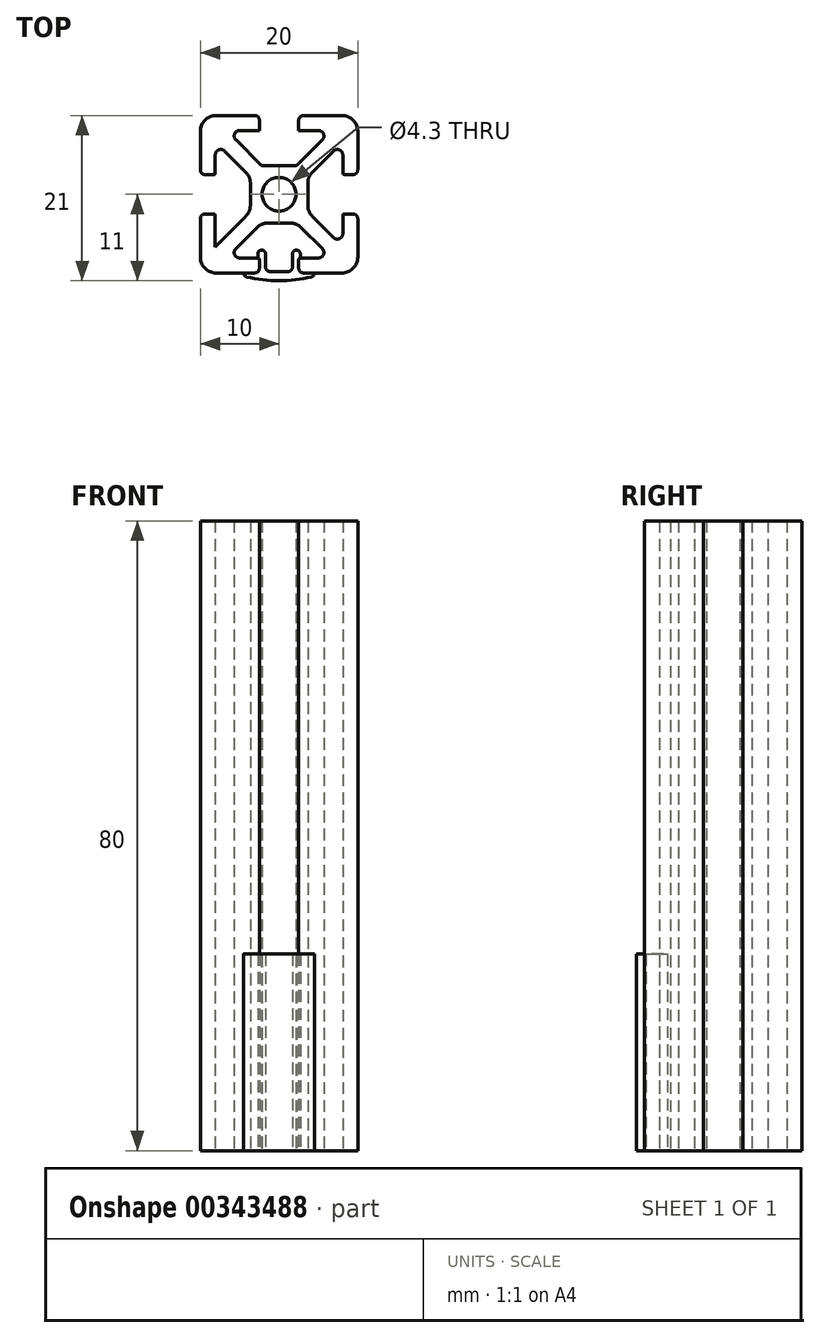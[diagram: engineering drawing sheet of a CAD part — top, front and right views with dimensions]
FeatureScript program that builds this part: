
annotation { "Feature Type Name" : "Feature", "Feature Type Description" : "" }
export const myFeature = defineFeature(function(context is Context, id is Id, definition is map)
    precondition{}
    {
        {
            var Q0;
            Q0=qCreatedBy(makeId("Top.planeOp"),FACE);
            var sketch = newSketch(context, id + "F0", { "sketchPlane" : qUnion([Q0])});
            skLineSegment(sketch, "E0.bottom", {"start": v(-8, 10) * mm, "end": v(-3.1, 10) * mm});
            skLineSegment(sketch, "E0.top", {"start": v(-8, -10) * mm, "end": v(-3.1, -10) * mm});
            skLineSegment(sketch, "E0.left", {"start": v(-10, 8) * mm, "end": v(-10, 3.1) * mm});
            skLineSegment(sketch, "E0.right", {"start": v(10, 8) * mm, "end": v(10, 3.1) * mm});
            skLineSegment(sketch, "E1", {"start": v(-10, 10) * mm, "end": v(10, -10) * mm, "construction": true});
            skLineSegment(sketch, "E2", {"start": v(10, 10) * mm, "end": v(-10, -10) * mm, "construction": true});
            skCircle(sketch, "E3", {"center": v(0, 0) * mm, "radius": 2.15 * mm});
            skLineSegment(sketch, "E4.bottom", {"start": v(-2.24, 3.65) * mm, "end": v(2.24, 3.65) * mm});
            skLineSegment(sketch, "E4.top", {"start": v(-1.4, -3.65) * mm, "end": v(1.4, -3.65) * mm});
            skLineSegment(sketch, "E4.left", {"start": v(-3.65, 1.4) * mm, "end": v(-3.65, -1.4) * mm});
            skLineSegment(sketch, "E4.right", {"start": v(3.65, 1.4) * mm, "end": v(3.65, -1.4) * mm});
            skLineSegment(sketch, "E5", {"start": v(-5.5, 6.9) * mm, "end": v(-2.24, 3.65) * mm});
            skLineSegment(sketch, "E6", {"start": v(-6.9, 5.5) * mm, "end": v(-4.24, 2.82) * mm});
            skLineSegment(sketch, "E7", {"start": v(5.5, 6.9) * mm, "end": v(2.24, 3.65) * mm});
            skLineSegment(sketch, "E8", {"start": v(6.9, 5.5) * mm, "end": v(4.24, 2.82) * mm});
            skLineSegment(sketch, "E9", {"start": v(-21.63, 0) * mm, "end": v(22.23, 0) * mm, "construction": true});
            skLineSegment(sketch, "E10.trimOffspring", {"start": v(-4.24, -2.82) * mm, "end": v(-8.1, -6.69) * mm});
            skLineSegment(sketch, "E11.trimOffspring", {"start": v(-2.82, -4.24) * mm, "end": v(-5.5, -6.9) * mm});
            skLineSegment(sketch, "E12.trimOffspring", {"start": v(2.82, -4.24) * mm, "end": v(5.5, -6.9) * mm});
            skLineSegment(sketch, "E13.trimOffspring", {"start": v(4.24, -2.82) * mm, "end": v(6.9, -5.5) * mm});
            skLineSegment(sketch, "E14", {"start": v(-8.1, 5) * mm, "end": v(-8.1, 2.7) * mm});
            skLineSegment(sketch, "E15", {"start": v(-8.3, 2.5) * mm, "end": v(-9.4, 2.5) * mm});
            skLineSegment(sketch, "E16", {"start": v(-8.3, -2.5) * mm, "end": v(-9.4, -2.5) * mm});
            skLineSegment(sketch, "E17.trimOffspring", {"start": v(-10, -3.1) * mm, "end": v(-10, -8) * mm});
            skLineSegment(sketch, "E18.trimOffspring", {"start": v(-8.1, -2.7) * mm, "end": v(-8.1, -6.69) * mm});
            skLineSegment(sketch, "E19", {"start": v(-5, 8.1) * mm, "end": v(-2.5, 8.1) * mm});
            skLineSegment(sketch, "E20", {"start": v(8.1, 5) * mm, "end": v(8.1, 2.7) * mm});
            skLineSegment(sketch, "E21", {"start": v(5, -8.1) * mm, "end": v(2.7, -8.1) * mm});
            skLineSegment(sketch, "E22", {"start": v(8.3, 2.5) * mm, "end": v(9.4, 2.5) * mm});
            skLineSegment(sketch, "E23", {"start": v(9.4, -2.5) * mm, "end": v(8.3, -2.5) * mm});
            skLineSegment(sketch, "E24.trimOffspring", {"start": v(10, -3.1) * mm, "end": v(10, -8) * mm});
            skLineSegment(sketch, "E25.trimOffspring", {"start": v(8.1, -2.7) * mm, "end": v(8.1, -5) * mm});
            skLineSegment(sketch, "E26", {"start": v(-2.5, 8.1) * mm, "end": v(-2.5, 9.4) * mm});
            skLineSegment(sketch, "E27", {"start": v(2.5, 8.1) * mm, "end": v(2.5, 9.4) * mm});
            skLineSegment(sketch, "E28", {"start": v(0, 10.9) * mm, "end": v(0, -13.43) * mm, "construction": true});
            skLineSegment(sketch, "E29.trimOffspring", {"start": v(3.1, 10) * mm, "end": v(8, 10) * mm});
            skLineSegment(sketch, "E30.trimOffspring", {"start": v(2.5, 8.1) * mm, "end": v(5, 8.1) * mm});
            skPoint(sketch, "E31.visualSharp", {"position": v(-10, 10) * mm});
            skArc(sketch, "E31.filletArc", {"start": v(-8, 10) * mm, "mid": v(-9.41, 9.41) * mm, "end": v(-10, 8) * mm});
            skPoint(sketch, "E32.visualSharp", {"position": v(10, 10) * mm});
            skArc(sketch, "E32.filletArc", {"start": v(10, 8) * mm, "mid": v(9.41, 9.41) * mm, "end": v(8, 10) * mm});
            skPoint(sketch, "E33.visualSharp", {"position": v(10, -10) * mm});
            skArc(sketch, "E33.filletArc", {"start": v(8, -10) * mm, "mid": v(9.41, -9.41) * mm, "end": v(10, -8) * mm});
            skPoint(sketch, "E34.visualSharp", {"position": v(-10, -10) * mm});
            skArc(sketch, "E34.filletArc", {"start": v(-10, -8) * mm, "mid": v(-9.41, -9.41) * mm, "end": v(-8, -10) * mm});
            skPoint(sketch, "E35.visualSharp", {"position": v(-3.65, 2.24) * mm});
            skArc(sketch, "E35.filletArc", {"start": v(-3.65, 1.4) * mm, "mid": v(-3.8, 2.17) * mm, "end": v(-4.24, 2.82) * mm});
            skPoint(sketch, "E36.visualSharp", {"position": v(-8.1, 6.69) * mm});
            skArc(sketch, "E36.filletArc", {"start": v(-6.9, 5.5) * mm, "mid": v(-7.67, 5.64) * mm, "end": v(-8.1, 5) * mm});
            skPoint(sketch, "E37.visualSharp", {"position": v(-6.69, 8.1) * mm});
            skArc(sketch, "E37.filletArc", {"start": v(-5, 8.1) * mm, "mid": v(-5.64, 7.67) * mm, "end": v(-5.5, 6.9) * mm});
            skPoint(sketch, "E38.visualSharp", {"position": v(6.69, 8.1) * mm});
            skArc(sketch, "E38.filletArc", {"start": v(5.5, 6.9) * mm, "mid": v(5.64, 7.67) * mm, "end": v(5, 8.1) * mm});
            skPoint(sketch, "E39.visualSharp", {"position": v(8.1, 6.69) * mm});
            skArc(sketch, "E39.filletArc", {"start": v(8.1, 5) * mm, "mid": v(7.67, 5.64) * mm, "end": v(6.9, 5.5) * mm});
            skPoint(sketch, "E40.visualSharp", {"position": v(8.1, -6.69) * mm});
            skArc(sketch, "E40.filletArc", {"start": v(6.9, -5.5) * mm, "mid": v(7.67, -5.64) * mm, "end": v(8.1, -5) * mm});
            skPoint(sketch, "E41.visualSharp", {"position": v(6.69, -8.1) * mm});
            skArc(sketch, "E41.filletArc", {"start": v(5, -8.1) * mm, "mid": v(5.64, -7.67) * mm, "end": v(5.5, -6.9) * mm});
            skPoint(sketch, "E42.visualSharp", {"position": v(-6.69, -8.1) * mm});
            skArc(sketch, "E42.filletArc", {"start": v(-5.5, -6.9) * mm, "mid": v(-5.64, -7.67) * mm, "end": v(-5, -8.1) * mm});
            skPoint(sketch, "E43.visualSharp", {"position": v(3.65, 2.24) * mm});
            skArc(sketch, "E43.filletArc", {"start": v(4.24, 2.82) * mm, "mid": v(3.8, 2.17) * mm, "end": v(3.65, 1.4) * mm});
            skPoint(sketch, "E44.visualSharp", {"position": v(3.65, -2.24) * mm});
            skArc(sketch, "E44.filletArc", {"start": v(3.65, -1.4) * mm, "mid": v(3.8, -2.17) * mm, "end": v(4.24, -2.82) * mm});
            skPoint(sketch, "E45.visualSharp", {"position": v(2.24, -3.65) * mm});
            skArc(sketch, "E45.filletArc", {"start": v(2.82, -4.24) * mm, "mid": v(2.17, -3.8) * mm, "end": v(1.4, -3.65) * mm});
            skPoint(sketch, "E46.visualSharp", {"position": v(-2.24, -3.65) * mm});
            skArc(sketch, "E46.filletArc", {"start": v(-1.4, -3.65) * mm, "mid": v(-2.17, -3.8) * mm, "end": v(-2.82, -4.24) * mm});
            skPoint(sketch, "E47.visualSharp", {"position": v(-3.65, -2.24) * mm});
            skArc(sketch, "E47.filletArc", {"start": v(-4.24, -2.82) * mm, "mid": v(-3.8, -2.17) * mm, "end": v(-3.65, -1.4) * mm});
            skLineSegment(sketch, "E48", {"start": v(-2.5, -9.4) * mm, "end": v(-2.5, -8.3) * mm});
            skLineSegment(sketch, "E49", {"start": v(2.5, -8.3) * mm, "end": v(2.5, -9.4) * mm});
            skLineSegment(sketch, "E50.trimOffspring", {"start": v(-2.7, -8.1) * mm, "end": v(-5, -8.1) * mm});
            skLineSegment(sketch, "E51.trimOffspring", {"start": v(3.1, -10) * mm, "end": v(8, -10) * mm});
            skPoint(sketch, "E52.visualSharp", {"position": v(-10, -2.5) * mm});
            skArc(sketch, "E52.filletArc", {"start": v(-9.4, -2.5) * mm, "mid": v(-9.82, -2.68) * mm, "end": v(-10, -3.1) * mm});
            skPoint(sketch, "E53.visualSharp", {"position": v(-10, 2.5) * mm});
            skArc(sketch, "E53.filletArc", {"start": v(-10, 3.1) * mm, "mid": v(-9.82, 2.68) * mm, "end": v(-9.4, 2.5) * mm});
            skPoint(sketch, "E54.visualSharp", {"position": v(10, -2.5) * mm});
            skArc(sketch, "E54.filletArc", {"start": v(10, -3.1) * mm, "mid": v(9.82, -2.68) * mm, "end": v(9.4, -2.5) * mm});
            skPoint(sketch, "E55.visualSharp", {"position": v(10, 2.5) * mm});
            skArc(sketch, "E55.filletArc", {"start": v(9.4, 2.5) * mm, "mid": v(9.82, 2.68) * mm, "end": v(10, 3.1) * mm});
            skPoint(sketch, "E56.visualSharp", {"position": v(2.5, -10) * mm});
            skArc(sketch, "E56.filletArc", {"start": v(2.5, -9.4) * mm, "mid": v(2.68, -9.82) * mm, "end": v(3.1, -10) * mm});
            skPoint(sketch, "E57.visualSharp", {"position": v(-2.5, -10) * mm});
            skArc(sketch, "E57.filletArc", {"start": v(-3.1, -10) * mm, "mid": v(-2.68, -9.82) * mm, "end": v(-2.5, -9.4) * mm});
            skPoint(sketch, "E58.visualSharp", {"position": v(-8.1, 2.5) * mm});
            skArc(sketch, "E58.filletArc", {"start": v(-8.3, 2.5) * mm, "mid": v(-8.16, 2.56) * mm, "end": v(-8.1, 2.7) * mm});
            skPoint(sketch, "E59.visualSharp", {"position": v(-8.1, -2.5) * mm});
            skArc(sketch, "E59.filletArc", {"start": v(-8.1, -2.7) * mm, "mid": v(-8.16, -2.56) * mm, "end": v(-8.3, -2.5) * mm});
            skPoint(sketch, "E60.visualSharp", {"position": v(-2.5, -8.1) * mm});
            skArc(sketch, "E60.filletArc", {"start": v(-2.5, -8.3) * mm, "mid": v(-2.56, -8.16) * mm, "end": v(-2.7, -8.1) * mm});
            skPoint(sketch, "E61.visualSharp", {"position": v(2.5, -8.1) * mm});
            skArc(sketch, "E61.filletArc", {"start": v(2.7, -8.1) * mm, "mid": v(2.56, -8.16) * mm, "end": v(2.5, -8.3) * mm});
            skPoint(sketch, "E62.visualSharp", {"position": v(8.1, -2.5) * mm});
            skArc(sketch, "E62.filletArc", {"start": v(8.3, -2.5) * mm, "mid": v(8.16, -2.56) * mm, "end": v(8.1, -2.7) * mm});
            skPoint(sketch, "E63.visualSharp", {"position": v(8.1, 2.5) * mm});
            skArc(sketch, "E63.filletArc", {"start": v(8.1, 2.7) * mm, "mid": v(8.16, 2.56) * mm, "end": v(8.3, 2.5) * mm});
            skPoint(sketch, "E64.visualSharp", {"position": v(-2.5, 10) * mm});
            skArc(sketch, "E64.filletArc", {"start": v(-2.5, 9.4) * mm, "mid": v(-2.68, 9.82) * mm, "end": v(-3.1, 10) * mm});
            skPoint(sketch, "E65.visualSharp", {"position": v(2.5, 10) * mm});
            skArc(sketch, "E65.filletArc", {"start": v(3.1, 10) * mm, "mid": v(2.68, 9.82) * mm, "end": v(2.5, 9.4) * mm});
            skSolve(sketch);
        }
        {
            var Q0;
            Q0 = qSketchRegion(id + "F0", true);
            extrude(context, id + "F1", {"entities" : qUnion([Q0]), "depth" : 80 * mm});
        }
        {
            var Q0;
            Q0=qCreatedBy(makeId("Top.planeOp"),FACE);
            var sketch = newSketch(context, id + "F2", { "sketchPlane" : qUnion([Q0])});
            skLineSegment(sketch, "E66.0", {"start": v(-2.7, -8.1) * mm, "end": v(-5, -8.1) * mm});
            skLineSegment(sketch, "E67.0", {"start": v(-2.5, -9.4) * mm, "end": v(-2.5, -8.3) * mm});
            skLineSegment(sketch, "E68.0", {"start": v(2.5, -8.3) * mm, "end": v(2.5, -9.4) * mm});
            skLineSegment(sketch, "E69.0", {"start": v(5, -8.1) * mm, "end": v(2.7, -8.1) * mm});
            skLineSegment(sketch, "E70.0", {"start": v(-8, -10) * mm, "end": v(-3.1, -10) * mm});
            skLineSegment(sketch, "E71.0", {"start": v(3.1, -10) * mm, "end": v(8, -10) * mm});
            skArc(sketch, "E72", {"start": v(-4.12, -10.5) * mm, "mid": v(0, -11) * mm, "end": v(4.12, -10.5) * mm});
            skPoint(sketch, "E72.first.point", {"position": v(-4.5, -10.4) * mm});
            skPoint(sketch, "E72.second.point", {"position": v(0, -11) * mm});
            skLineSegment(sketch, "E73.top", {"start": v(-1.2, -9.8) * mm, "end": v(1.2, -9.8) * mm});
            skLineSegment(sketch, "E73.left", {"start": v(-1.7, -7.6) * mm, "end": v(-1.7, -9.3) * mm});
            skLineSegment(sketch, "E73.right", {"start": v(1.7, -7.6) * mm, "end": v(1.7, -9.3) * mm});
            skLineSegment(sketch, "E74", {"start": v(0, 0) * mm, "end": v(0, -12.98) * mm, "construction": true});
            skLineSegment(sketch, "E75", {"start": v(-2.7, -7.6) * mm, "end": v(-2.7, -8.1) * mm});
            skLineSegment(sketch, "E76", {"start": v(-2.2, -7.1) * mm, "end": v(-2.2, -7.1) * mm});
            skArc(sketch, "E77.0", {"start": v(-2.5, -8.3) * mm, "mid": v(-2.56, -8.16) * mm, "end": v(-2.7, -8.1) * mm});
            skLineSegment(sketch, "E78", {"start": v(2.2, -7.1) * mm, "end": v(2.2, -7.1) * mm});
            skPoint(sketch, "E79.0", {"position": v(2.56, -8.16) * mm});
            skArc(sketch, "E80.0", {"start": v(2.7, -8.1) * mm, "mid": v(2.56, -8.16) * mm, "end": v(2.5, -8.3) * mm});
            skArc(sketch, "E81", {"start": v(2.5, -8.3) * mm, "mid": v(2.56, -8.16) * mm, "end": v(2.7, -8.1) * mm});
            skLineSegment(sketch, "E82", {"start": v(2.7, -8.1) * mm, "end": v(2.7, -7.6) * mm});
            skArc(sketch, "E83.0", {"start": v(-3.1, -10) * mm, "mid": v(-2.68, -9.82) * mm, "end": v(-2.5, -9.4) * mm});
            skArc(sketch, "E84.0", {"start": v(2.5, -9.4) * mm, "mid": v(2.68, -9.82) * mm, "end": v(3.1, -10) * mm});
            skPoint(sketch, "E85.visualSharp", {"position": v(-1.7, -7.1) * mm});
            skArc(sketch, "E85.filletArc", {"start": v(-1.7, -7.6) * mm, "mid": v(-1.85, -7.25) * mm, "end": v(-2.2, -7.1) * mm});
            skPoint(sketch, "E86.visualSharp", {"position": v(-2.7, -7.1) * mm});
            skArc(sketch, "E86.filletArc", {"start": v(-2.2, -7.1) * mm, "mid": v(-2.55, -7.25) * mm, "end": v(-2.7, -7.6) * mm});
            skPoint(sketch, "E87.visualSharp", {"position": v(1.7, -7.1) * mm});
            skArc(sketch, "E87.filletArc", {"start": v(2.2, -7.1) * mm, "mid": v(1.85, -7.25) * mm, "end": v(1.7, -7.6) * mm});
            skPoint(sketch, "E88.visualSharp", {"position": v(2.7, -7.1) * mm});
            skArc(sketch, "E88.filletArc", {"start": v(2.7, -7.6) * mm, "mid": v(2.55, -7.25) * mm, "end": v(2.2, -7.1) * mm});
            skPoint(sketch, "E89.visualSharp", {"position": v(-1.7, -9.8) * mm});
            skArc(sketch, "E89.filletArc", {"start": v(-1.7, -9.3) * mm, "mid": v(-1.55, -9.65) * mm, "end": v(-1.2, -9.8) * mm});
            skPoint(sketch, "E90.visualSharp", {"position": v(1.7, -9.8) * mm});
            skArc(sketch, "E90.filletArc", {"start": v(1.2, -9.8) * mm, "mid": v(1.55, -9.65) * mm, "end": v(1.7, -9.3) * mm});
            skLineSegment(sketch, "E91", {"start": v(-4.5, -10) * mm, "end": v(-4.5, -10.01) * mm});
            skLineSegment(sketch, "E92", {"start": v(4.5, -10.01) * mm, "end": v(4.5, -10) * mm});
            skArc(sketch, "E93.filletArc", {"start": v(-4.5, -10.01) * mm, "mid": v(-4.4, -10.32) * mm, "end": v(-4.12, -10.5) * mm});
            skPoint(sketch, "E94.visualSharp", {"position": v(4.5, -10.4) * mm});
            skArc(sketch, "E94.filletArc", {"start": v(4.12, -10.5) * mm, "mid": v(4.4, -10.32) * mm, "end": v(4.5, -10.01) * mm});
            skSolve(sketch);
        }
        {
            var Q0;
            Q0 = qSketchRegion(id + "F2", true);
            extrude(context, id + "F3", {"entities" : qUnion([Q0]), "depth" : 25 * mm});
        }
    });
